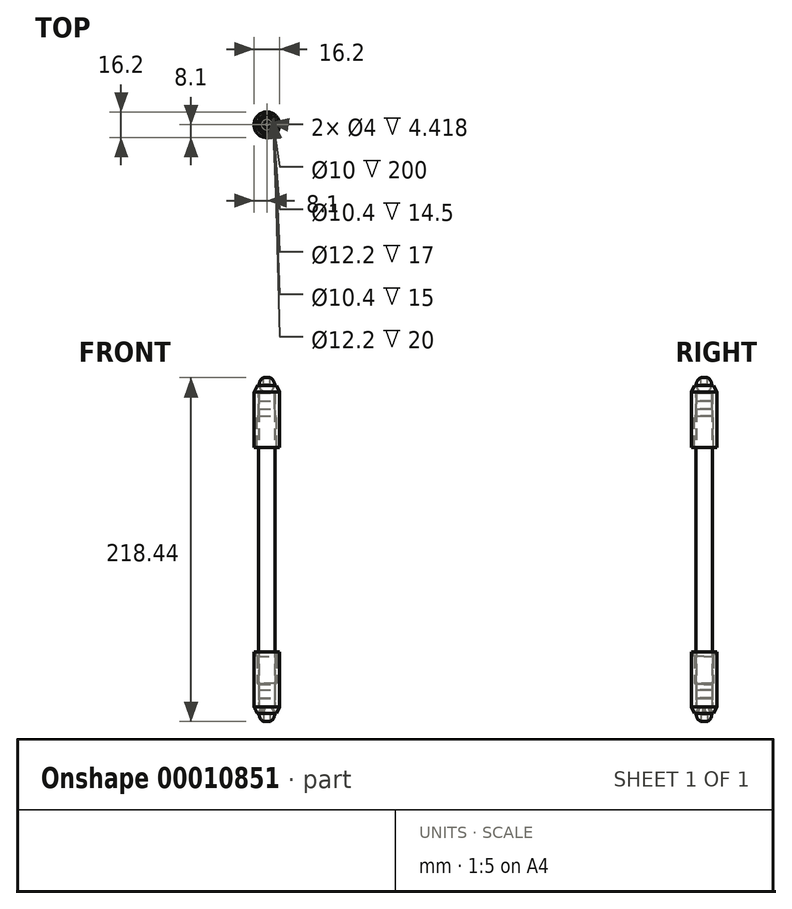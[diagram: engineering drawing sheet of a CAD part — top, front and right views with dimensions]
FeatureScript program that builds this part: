
annotation { "Feature Type Name" : "Feature", "Feature Type Description" : "" }
export const myFeature = defineFeature(function(context is Context, id is Id, definition is map)
    precondition{}
    {
        {
            var Q0;
            Q0=qCreatedBy(makeId("Front.planeOp"),FACE);
            var sketch = newSketch(context, id + "F0", { "sketchPlane" : qUnion([Q0])});
            skLineSegment(sketch, "E0", {"start": v(-5.03, 0.7) * mm, "end": v(-6.03, 0.7) * mm});
            skLineSegment(sketch, "E1", {"start": v(-8.1, 4.8) * mm, "end": v(-8.1, 39.8) * mm});
            skLineSegment(sketch, "E2", {"start": v(-8.1, 39.8) * mm, "end": v(-6.1, 39.8) * mm});
            skLineSegment(sketch, "E3", {"start": v(-6.1, 39.8) * mm, "end": v(-6.1, 19.8) * mm});
            skLineSegment(sketch, "E4", {"start": v(-6.1, 19.8) * mm, "end": v(-5.2, 19.8) * mm});
            skLineSegment(sketch, "E5", {"start": v(-5.2, 19.8) * mm, "end": v(-5.2, 4.8) * mm});
            skLineSegment(sketch, "E6", {"start": v(-5.2, 4.8) * mm, "end": v(-3.11, 4.8) * mm});
            skLineSegment(sketch, "E7", {"start": v(0, 5.2) * mm, "end": v(0, 4.8) * mm});
            skLineSegment(sketch, "E8", {"start": v(-6.03, 0.7) * mm, "end": v(-8.1, 4.8) * mm});
            skLineSegment(sketch, "E9", {"start": v(0, 0) * mm, "end": v(0, 32.36) * mm, "construction": true});
            skLineSegment(sketch, "E10", {"start": v(2.85, 3.2) * mm, "end": v(-9.79, 3.2) * mm, "construction": true});
            skCircle(sketch, "E11", {"center": v(0, 0) * mm, "radius": 4.85 * mm});
            skLineSegment(sketch, "E12", {"start": v(0, 4.8) * mm, "end": v(0, -4.85) * mm});
            skLineSegment(sketch, "E13", {"start": v(0, 15.55) * mm, "end": v(-5, 15.55) * mm});
            skLineSegment(sketch, "E14", {"start": v(-5, 15.55) * mm, "end": v(-5, 10.55) * mm});
            skLineSegment(sketch, "E15", {"start": v(-5, 10.55) * mm, "end": v(0, 10.55) * mm});
            skLineSegment(sketch, "E16", {"start": v(0, 10.55) * mm, "end": v(0, 15.55) * mm});
            skLineSegment(sketch, "E17", {"start": v(0, 5.3) * mm, "end": v(-5, 5.3) * mm});
            skLineSegment(sketch, "E18", {"start": v(-5, 5.3) * mm, "end": v(-5, 10.3) * mm});
            skLineSegment(sketch, "E19", {"start": v(-5, 10.3) * mm, "end": v(0, 10.3) * mm});
            skLineSegment(sketch, "E20", {"start": v(0, 10.3) * mm, "end": v(0, 5.3) * mm});
            skLineSegment(sketch, "E21", {"start": v(-4, 2.74) * mm, "end": v(4, 2.74) * mm, "construction": true});
            skLineSegment(sketch, "E22", {"start": v(0, 11.48) * mm, "end": v(-8.67, -7.13) * mm, "construction": true});
            skLineSegment(sketch, "E23", {"start": v(-5.03, 0.7) * mm, "end": v(-3.11, 4.8) * mm});
            skPoint(sketch, "E24", {"position": v(-4.4, 2.05) * mm});
            skSolve(sketch);
        }
        {
            var Q0;
            Q0=makeQuery(id+"F0.imprint","IMPRINT",FACE,{"disambiguationData":[TD([[makeQuery(id+"F0.imprint","IMPRINT",EDGE,{"derivedFrom":sQuery(id+"F0.wireOp",EDGE,"E13")}),1.0]])]});
            var Q1;
            Q1=makeQuery(id+"F0.imprint","IMPRINT",FACE,{"disambiguationData":[TD([[makeQuery(id+"F0.imprint","IMPRINT",EDGE,{"derivedFrom":sQuery(id+"F0.wireOp",EDGE,"E17")}),-1.0]])]});
            var Q2;
            {var subQ0=sQuery(id+"F0.wireOp",EDGE,"E12");Q2=makeQuery(id+"F0.imprint","IMPRINT",FACE,{"disambiguationData":[TD([[makeQuery(id+"F0.imprint","IMPRINT",EDGE,{"derivedFrom":subQ0}),-1.0]])]});}
            var Q3;
            {var subQ0=sQuery(id+"F0.wireOp",EDGE,"E0");Q3=makeQuery(id+"F0.imprint","IMPRINT",FACE,{"disambiguationData":[TD([[makeQuery(id+"F0.imprint","IMPRINT",EDGE,{"derivedFrom":subQ0}),-1.0]])]});}
            var Q4;
            Q4=sQuery(id+"F0.wireOp",EDGE,"E9");
            revolve(context, id + "F1", {"entities" : qUnion([Q0, Q1, Q2, Q3]), "axis" : qUnion([Q4]), "revolveType" : RevolveType.FULL});
        }
        {
            var Q0;
            Q0=makeQuery(id+"F1.opRevolve","SWEPT_FACE",FACE,{"disambiguationData":[OSD([sQuery(id+"F0.wireOp",EDGE,"E6")])]});
            var sketch = newSketch(context, id + "F2", { "sketchPlane" : qUnion([Q0])});
            skCircle(sketch, "E25", {"center": v(0, 0) * mm, "radius": 6 * mm});
            skCircle(sketch, "E26", {"center": v(0, 0) * mm, "radius": 5 * mm});
            skSolve(sketch);
        }
        {
            var Q0;
            Q0=makeQuery(id+"F2.imprint","IMPRINT",FACE,{"disambiguationData":[TD([[makeQuery(id+"F2.imprint","IMPRINT",EDGE,{"derivedFrom":sQuery(id+"F2.wireOp",EDGE,"E26")}),-1.0]])]});
            extrude(context, id + "F3", {"entities" : qUnion([Q0]), "depth" : 200 * mm});
        }
        {
            var Q0;
            Q0=makeQuery(id+"F3.opExtrude","CAP_FACE",FACE,{"disambiguationData":[OSD([sQuery(id+"F0.wireOp",EDGE,"E4"),sQuery(id+"F0.wireOp",EDGE,"E5"),sQuery(id+"F2.wireOp",EDGE,"E26")])],"isStart":false});
            cPlane(context, id + "F4", {"entities" : qUnion([Q0]), "cplaneType" : CPlaneType.OFFSET, "offset" : 100 * mm, "oppositeDirection" : true, "width" : 150 * mm, "height" : 150 * mm});
        }
        {
            var Q0;
            Q0=qCreatedBy(makeId("Top.planeOp"),FACE);
            cPlane(context, id + "F5", {"entities" : qUnion([Q0]), "cplaneType" : CPlaneType.OFFSET, "offset" : 5 * mm, "oppositeDirection" : true, "width" : 150 * mm, "height" : 150 * mm});
        }
        {
            var Q0;
            Q0=qCreatedBy(id+"F5.planeOp",FACE);
            var sketch = newSketch(context, id + "F6", { "sketchPlane" : qUnion([Q0])});
            skCircle(sketch, "E27", {"center": v(0, 0) * mm, "radius": 2 * mm});
            skSolve(sketch);
        }
        {
            var Q0;
            Q0=makeQuery(id+"F6.imprint","IMPRINT",FACE,{"disambiguationData":[TD([[makeQuery(id+"F6.imprint","IMPRINT",EDGE,{"derivedFrom":sQuery(id+"F6.wireOp",EDGE,"E27")}),1.0]])]});
            extrude(context, id + "F7", {"entities" : qUnion([Q0]), "operationType" : NewBodyOperationType.REMOVE, "depth" : 5 * mm});
        }
        {
            var Q0;
            Q0=makeQuery(id+"F1.opRevolve","SWEPT_BODY",BODY,{"disambiguationData":[OSD([sQuery(id+"F0.wireOp",EDGE,"E17"),sQuery(id+"F0.wireOp",EDGE,"E18"),sQuery(id+"F0.wireOp",EDGE,"E19"),sQuery(id+"F0.wireOp",EDGE,"E20")])]});
            var Q1;
            Q1=makeQuery(id+"F1.opRevolve","SWEPT_BODY",BODY,{"disambiguationData":[OSD([sQuery(id+"F0.wireOp",EDGE,"E13"),sQuery(id+"F0.wireOp",EDGE,"E14"),sQuery(id+"F0.wireOp",EDGE,"E15"),sQuery(id+"F0.wireOp",EDGE,"E16")])]});
            var Q2;
            Q2=makeQuery(id+"F1.opRevolve","SWEPT_BODY",BODY,{"disambiguationData":[OSD([sQuery(id+"F0.wireOp",EDGE,"E11"),sQuery(id+"F0.wireOp",EDGE,"E12")])]});
            var Q3;
            Q3=makeQuery(id+"F1.opRevolve","SWEPT_BODY",BODY,{"disambiguationData":[OSD([sQuery(id+"F0.wireOp",EDGE,"841e1b56-2235-48bc-aee3-342361c37d41"),sQuery(id+"F0.wireOp",EDGE,"E0"),sQuery(id+"F0.wireOp",EDGE,"E1"),sQuery(id+"F0.wireOp",EDGE,"E2"),sQuery(id+"F0.wireOp",EDGE,"E3"),sQuery(id+"F0.wireOp",EDGE,"E4"),sQuery(id+"F0.wireOp",EDGE,"E5"),sQuery(id+"F0.wireOp",EDGE,"E6"),sQuery(id+"F0.wireOp",EDGE,"E8"),sQuery(id+"F0.wireOp",EDGE,"4b548780-3497-4359-ae85-f4aefd225b06")])]});
            var Q4;
            Q4=qCreatedBy(id+"F4.planeOp",FACE);
            mirror(context, id + "F8", {"entities" : qUnion([Q0, Q1, Q2, Q3]), "mirrorPlane" : qUnion([Q4])});
        }
        {
            var Q0;
            Q0=makeQuery(id+"F1.opRevolve","SWEPT_EDGE",EDGE,{"disambiguationData":[OSD([sQuery(id+"F0.wireOp",EDGE,"E2"),sQuery(id+"F0.wireOp",EDGE,"E3")])]});
            var Q1;
            Q1=makeQuery(id+"F1.opRevolve","SWEPT_EDGE",EDGE,{"disambiguationData":[OSD([sQuery(id+"F0.wireOp",EDGE,"E2"),sQuery(id+"F0.wireOp",EDGE,"E3")])]});
            chamfer(context, id + "F9", {"entities" : qUnion([Q0, Q1]), "chamferType" : ChamferType.TWO_OFFSETS, "width1" : 1 * mm, "oppositeDirection" : false, "width2" : 3 * mm, "tangentPropagation" : true});
        }
        {
            var Q0;
            Q0=qCreatedBy(makeId("Front.planeOp"),FACE);
            var sketch = newSketch(context, id + "F10", { "sketchPlane" : qUnion([Q0])});
            skLineSegment(sketch, "E28", {"start": v(-5.5, 0.7) * mm, "end": v(-3.6, 4.8) * mm});
            skLineSegment(sketch, "E29", {"start": v(-5.5, 0.7) * mm, "end": v(-4.14, 0.7) * mm});
            skLineSegment(sketch, "E30", {"start": v(-4.14, 0.7) * mm, "end": v(-2.47, 4.8) * mm});
            skLineSegment(sketch, "E31", {"start": v(-2.47, 4.8) * mm, "end": v(-3.6, 4.8) * mm});
            skLineSegment(sketch, "E32", {"start": v(0, 0) * mm, "end": v(0, -5.1) * mm, "construction": true});
            skSolve(sketch);
        }
        {
            var Q0;
            Q0=makeQuery(id+"F10.imprint","IMPRINT",FACE,{"disambiguationData":[TD([[makeQuery(id+"F10.imprint","IMPRINT",EDGE,{"derivedFrom":sQuery(id+"F10.wireOp",EDGE,"E28")}),-1.0]])]});
            var Q1;
            Q1=sQuery(id+"F10.wireOp",EDGE,"E32");
            revolve(context, id + "F11", {"entities" : qUnion([Q0]), "axis" : qUnion([Q1]), "revolveType" : RevolveType.SYMMETRIC, "angle" : 108 * degree});
        }
        {
            var Q0;
            Q0=makeQuery(id+"F11.opRevolve","SWEPT_BODY",BODY,{"disambiguationData":[OSD([sQuery(id+"F10.wireOp",EDGE,"E28"),sQuery(id+"F10.wireOp",EDGE,"E29"),sQuery(id+"F10.wireOp",EDGE,"E30"),sQuery(id+"F10.wireOp",EDGE,"E31")])]});
            var Q1;
            Q1=sQuery(id+"F10.wireOp",EDGE,"E32");
            circularPattern(context, id + "F12", {"entities" : qUnion([Q0]), "axis" : qUnion([Q1]), "angle" : 120 * degree, "instanceCount" : 3, "computeTransformsWithoutBuiltin" : true});
        }
        {
            var Q0;
            Q0=makeQuery(id+"F11.opRevolve","SWEPT_BODY",BODY,{"disambiguationData":[OSD([sQuery(id+"F10.wireOp",EDGE,"E28"),sQuery(id+"F10.wireOp",EDGE,"E29"),sQuery(id+"F10.wireOp",EDGE,"E30"),sQuery(id+"F10.wireOp",EDGE,"E31")])]});
            var Q1;
            Q1=makeQuery(id+"F12.opPattern","COPY",BODY,{"derivedFrom":makeQuery(id+"F11.opRevolve","SWEPT_BODY",BODY,{"disambiguationData":[OSD([sQuery(id+"F10.wireOp",EDGE,"E28"),sQuery(id+"F10.wireOp",EDGE,"E29"),sQuery(id+"F10.wireOp",EDGE,"E30"),sQuery(id+"F10.wireOp",EDGE,"E31")])]}),"instanceName":"2"});
            var Q2;
            Q2=makeQuery(id+"F12.opPattern","COPY",BODY,{"derivedFrom":makeQuery(id+"F11.opRevolve","SWEPT_BODY",BODY,{"disambiguationData":[OSD([sQuery(id+"F10.wireOp",EDGE,"E28"),sQuery(id+"F10.wireOp",EDGE,"E29"),sQuery(id+"F10.wireOp",EDGE,"E30"),sQuery(id+"F10.wireOp",EDGE,"E31")])]}),"instanceName":"1"});
            var Q3;
            Q3=makeQuery(id+"F1.opRevolve","SWEPT_BODY",BODY,{"disambiguationData":[OSD([sQuery(id+"F0.wireOp",EDGE,"E0"),sQuery(id+"F0.wireOp",EDGE,"E1"),sQuery(id+"F0.wireOp",EDGE,"E2"),sQuery(id+"F0.wireOp",EDGE,"E3"),sQuery(id+"F0.wireOp",EDGE,"E5"),sQuery(id+"F0.wireOp",EDGE,"E6"),sQuery(id+"F0.wireOp",EDGE,"E8"),sQuery(id+"F0.wireOp",EDGE,"E23")])]});
            booleanBodies(context, id + "F13", {"operationType" : BooleanOperationType.SUBTRACTION, "tools" : qUnion([Q0, Q1, Q2]), "targets" : qUnion([Q3])});
        }
        {
            var Q0;
            Q0=makeQuery(id+"F13.opBoolean","COPY",EDGE,{"derivedFrom":makeQuery(id+"F11.opRevolve","CAP_EDGE",EDGE,{"disambiguationData":[OSD([sQuery(id+"F10.wireOp",EDGE,"E28")])],"isStart":true})});
            var Q1;
            Q1=makeQuery(id+"F13.opBoolean","COPY",EDGE,{"derivedFrom":makeQuery(id+"F12.opPattern","COPY",EDGE,{"derivedFrom":makeQuery(id+"F11.opRevolve","CAP_EDGE",EDGE,{"disambiguationData":[OSD([sQuery(id+"F10.wireOp",EDGE,"E28")])],"isStart":false}),"instanceName":"2"})});
            var Q2;
            Q2=makeQuery(id+"F13.opBoolean","COPY",EDGE,{"derivedFrom":makeQuery(id+"F12.opPattern","COPY",EDGE,{"derivedFrom":makeQuery(id+"F11.opRevolve","CAP_EDGE",EDGE,{"disambiguationData":[OSD([sQuery(id+"F10.wireOp",EDGE,"E28")])],"isStart":true}),"instanceName":"1"})});
            var Q3;
            Q3=makeQuery(id+"F13.opBoolean","COPY",EDGE,{"derivedFrom":makeQuery(id+"F11.opRevolve","CAP_EDGE",EDGE,{"disambiguationData":[OSD([sQuery(id+"F10.wireOp",EDGE,"E28")])],"isStart":false})});
            var Q4;
            Q4=makeQuery(id+"F13.opBoolean","COPY",EDGE,{"derivedFrom":makeQuery(id+"F12.opPattern","COPY",EDGE,{"derivedFrom":makeQuery(id+"F11.opRevolve","CAP_EDGE",EDGE,{"disambiguationData":[OSD([sQuery(id+"F10.wireOp",EDGE,"E28")])],"isStart":true}),"instanceName":"2"})});
            var Q5;
            Q5=makeQuery(id+"F13.opBoolean","COPY",EDGE,{"derivedFrom":makeQuery(id+"F12.opPattern","COPY",EDGE,{"derivedFrom":makeQuery(id+"F11.opRevolve","CAP_EDGE",EDGE,{"disambiguationData":[OSD([sQuery(id+"F10.wireOp",EDGE,"E28")])],"isStart":false}),"instanceName":"1"})});
            fillet(context, id + "F14", {"entities" : qUnion([Q0, Q1, Q2, Q3, Q4, Q5]), "radius" : 0.5 * mm, "tangentPropagation" : true, "allowEdgeOverflow" : false});
        }
        {
            var Q0;
            {var subQ0=sQuery(id+"F10.wireOp",EDGE,"E31");var subQ1=sQuery(id+"F10.wireOp",EDGE,"E30");var subQ2=sQuery(id+"F10.wireOp",EDGE,"E29");var subQ3=sQuery(id+"F10.wireOp",EDGE,"E28");Q0=makeQuery(id+"F14.opFillet","BLEND_EDGE",EDGE,{"blendedFrom":[makeQuery(id+"F13.opBoolean","COPY",EDGE,{"derivedFrom":makeQuery(id+"F11.opRevolve","CAP_EDGE",EDGE,{"disambiguationData":[OSD([subQ3])],"isStart":true})}),makeQuery(id+"F13.opBoolean","SPLIT",FACE,{"disambiguationData":[TD([makeQuery(id+"F11.opRevolve","CAP_FACE",FACE,{"disambiguationData":[OSD([subQ3,subQ2,subQ1,subQ0])],"isStart":true})])],"derivedFrom":makeQuery(id+"F1.opRevolve","SWEPT_FACE",FACE,{"disambiguationData":[OSD([sQuery(id+"F0.wireOp",EDGE,"E23")])]})})],"blendedInto":[makeQuery(id+"F13.opBoolean","SPLIT",FACE,{"disambiguationData":[TD([makeQuery(id+"F11.opRevolve","CAP_FACE",FACE,{"disambiguationData":[OSD([subQ3,subQ2,subQ1,subQ0])],"isStart":true})])],"derivedFrom":makeQuery(id+"F1.opRevolve","SWEPT_FACE",FACE,{"disambiguationData":[OSD([sQuery(id+"F0.wireOp",EDGE,"E23")])]})})]});}
            var Q1;
            {var subQ0=sQuery(id+"F10.wireOp",EDGE,"E31");var subQ1=sQuery(id+"F10.wireOp",EDGE,"E30");var subQ2=sQuery(id+"F10.wireOp",EDGE,"E29");var subQ3=sQuery(id+"F10.wireOp",EDGE,"E28");Q1=makeQuery(id+"F14.opFillet","BLEND_EDGE",EDGE,{"blendedFrom":[makeQuery(id+"F13.opBoolean","COPY",EDGE,{"derivedFrom":makeQuery(id+"F12.opPattern","COPY",EDGE,{"derivedFrom":makeQuery(id+"F11.opRevolve","CAP_EDGE",EDGE,{"disambiguationData":[OSD([subQ3])],"isStart":false}),"instanceName":"2"})}),makeQuery(id+"F13.opBoolean","SPLIT",FACE,{"disambiguationData":[TD([makeQuery(id+"F11.opRevolve","CAP_FACE",FACE,{"disambiguationData":[OSD([subQ3,subQ2,subQ1,subQ0])],"isStart":true})])],"derivedFrom":makeQuery(id+"F1.opRevolve","SWEPT_FACE",FACE,{"disambiguationData":[OSD([sQuery(id+"F0.wireOp",EDGE,"E23")])]})})],"blendedInto":[makeQuery(id+"F13.opBoolean","SPLIT",FACE,{"disambiguationData":[TD([makeQuery(id+"F11.opRevolve","CAP_FACE",FACE,{"disambiguationData":[OSD([subQ3,subQ2,subQ1,subQ0])],"isStart":true})])],"derivedFrom":makeQuery(id+"F1.opRevolve","SWEPT_FACE",FACE,{"disambiguationData":[OSD([sQuery(id+"F0.wireOp",EDGE,"E23")])]})})]});}
            var Q2;
            {var subQ0=sQuery(id+"F10.wireOp",EDGE,"E31");var subQ1=sQuery(id+"F10.wireOp",EDGE,"E30");var subQ2=sQuery(id+"F10.wireOp",EDGE,"E29");var subQ3=sQuery(id+"F10.wireOp",EDGE,"E28");Q2=makeQuery(id+"F14.opFillet","BLEND_EDGE",EDGE,{"blendedFrom":[makeQuery(id+"F13.opBoolean","COPY",EDGE,{"derivedFrom":makeQuery(id+"F12.opPattern","COPY",EDGE,{"derivedFrom":makeQuery(id+"F11.opRevolve","CAP_EDGE",EDGE,{"disambiguationData":[OSD([subQ3])],"isStart":true}),"instanceName":"1"})}),makeQuery(id+"F13.opBoolean","SPLIT",FACE,{"disambiguationData":[TD([makeQuery(id+"F11.opRevolve","CAP_FACE",FACE,{"disambiguationData":[OSD([subQ3,subQ2,subQ1,subQ0])],"isStart":false})])],"derivedFrom":makeQuery(id+"F1.opRevolve","SWEPT_FACE",FACE,{"disambiguationData":[OSD([sQuery(id+"F0.wireOp",EDGE,"E23")])]})})],"blendedInto":[makeQuery(id+"F13.opBoolean","SPLIT",FACE,{"disambiguationData":[TD([makeQuery(id+"F11.opRevolve","CAP_FACE",FACE,{"disambiguationData":[OSD([subQ3,subQ2,subQ1,subQ0])],"isStart":false})])],"derivedFrom":makeQuery(id+"F1.opRevolve","SWEPT_FACE",FACE,{"disambiguationData":[OSD([sQuery(id+"F0.wireOp",EDGE,"E23")])]})})]});}
            var Q3;
            {var subQ0=sQuery(id+"F10.wireOp",EDGE,"E31");var subQ1=sQuery(id+"F10.wireOp",EDGE,"E30");var subQ2=sQuery(id+"F10.wireOp",EDGE,"E29");var subQ3=sQuery(id+"F10.wireOp",EDGE,"E28");Q3=makeQuery(id+"F14.opFillet","BLEND_EDGE",EDGE,{"blendedFrom":[makeQuery(id+"F13.opBoolean","COPY",EDGE,{"derivedFrom":makeQuery(id+"F11.opRevolve","CAP_EDGE",EDGE,{"disambiguationData":[OSD([subQ3])],"isStart":false})}),makeQuery(id+"F13.opBoolean","SPLIT",FACE,{"disambiguationData":[TD([makeQuery(id+"F11.opRevolve","CAP_FACE",FACE,{"disambiguationData":[OSD([subQ3,subQ2,subQ1,subQ0])],"isStart":false})])],"derivedFrom":makeQuery(id+"F1.opRevolve","SWEPT_FACE",FACE,{"disambiguationData":[OSD([sQuery(id+"F0.wireOp",EDGE,"E23")])]})})],"blendedInto":[makeQuery(id+"F13.opBoolean","SPLIT",FACE,{"disambiguationData":[TD([makeQuery(id+"F11.opRevolve","CAP_FACE",FACE,{"disambiguationData":[OSD([subQ3,subQ2,subQ1,subQ0])],"isStart":false})])],"derivedFrom":makeQuery(id+"F1.opRevolve","SWEPT_FACE",FACE,{"disambiguationData":[OSD([sQuery(id+"F0.wireOp",EDGE,"E23")])]})})]});}
            var Q4;
            {var subQ0=sQuery(id+"F10.wireOp",EDGE,"E31");var subQ1=sQuery(id+"F10.wireOp",EDGE,"E30");var subQ2=sQuery(id+"F10.wireOp",EDGE,"E29");var subQ3=sQuery(id+"F10.wireOp",EDGE,"E28");Q4=makeQuery(id+"F14.opFillet","BLEND_EDGE",EDGE,{"blendedFrom":[makeQuery(id+"F13.opBoolean","COPY",EDGE,{"derivedFrom":makeQuery(id+"F12.opPattern","COPY",EDGE,{"derivedFrom":makeQuery(id+"F11.opRevolve","CAP_EDGE",EDGE,{"disambiguationData":[OSD([subQ3])],"isStart":false}),"instanceName":"1"})}),makeQuery(id+"F13.opBoolean","SPLIT",FACE,{"disambiguationData":[TD([makeQuery(id+"F12.opPattern","COPY",FACE,{"derivedFrom":makeQuery(id+"F11.opRevolve","CAP_FACE",FACE,{"disambiguationData":[OSD([subQ3,subQ2,subQ1,subQ0])],"isStart":false}),"instanceName":"1"})])],"derivedFrom":makeQuery(id+"F1.opRevolve","SWEPT_FACE",FACE,{"disambiguationData":[OSD([sQuery(id+"F0.wireOp",EDGE,"E23")])]})})],"blendedInto":[makeQuery(id+"F13.opBoolean","SPLIT",FACE,{"disambiguationData":[TD([makeQuery(id+"F12.opPattern","COPY",FACE,{"derivedFrom":makeQuery(id+"F11.opRevolve","CAP_FACE",FACE,{"disambiguationData":[OSD([subQ3,subQ2,subQ1,subQ0])],"isStart":false}),"instanceName":"1"})])],"derivedFrom":makeQuery(id+"F1.opRevolve","SWEPT_FACE",FACE,{"disambiguationData":[OSD([sQuery(id+"F0.wireOp",EDGE,"E23")])]})})]});}
            var Q5;
            {var subQ0=sQuery(id+"F10.wireOp",EDGE,"E31");var subQ1=sQuery(id+"F10.wireOp",EDGE,"E30");var subQ2=sQuery(id+"F10.wireOp",EDGE,"E29");var subQ3=sQuery(id+"F10.wireOp",EDGE,"E28");Q5=makeQuery(id+"F14.opFillet","BLEND_EDGE",EDGE,{"blendedFrom":[makeQuery(id+"F13.opBoolean","COPY",EDGE,{"derivedFrom":makeQuery(id+"F12.opPattern","COPY",EDGE,{"derivedFrom":makeQuery(id+"F11.opRevolve","CAP_EDGE",EDGE,{"disambiguationData":[OSD([subQ3])],"isStart":true}),"instanceName":"2"})}),makeQuery(id+"F13.opBoolean","SPLIT",FACE,{"disambiguationData":[TD([makeQuery(id+"F12.opPattern","COPY",FACE,{"derivedFrom":makeQuery(id+"F11.opRevolve","CAP_FACE",FACE,{"disambiguationData":[OSD([subQ3,subQ2,subQ1,subQ0])],"isStart":false}),"instanceName":"1"})])],"derivedFrom":makeQuery(id+"F1.opRevolve","SWEPT_FACE",FACE,{"disambiguationData":[OSD([sQuery(id+"F0.wireOp",EDGE,"E23")])]})})],"blendedInto":[makeQuery(id+"F13.opBoolean","SPLIT",FACE,{"disambiguationData":[TD([makeQuery(id+"F12.opPattern","COPY",FACE,{"derivedFrom":makeQuery(id+"F11.opRevolve","CAP_FACE",FACE,{"disambiguationData":[OSD([subQ3,subQ2,subQ1,subQ0])],"isStart":false}),"instanceName":"1"})])],"derivedFrom":makeQuery(id+"F1.opRevolve","SWEPT_FACE",FACE,{"disambiguationData":[OSD([sQuery(id+"F0.wireOp",EDGE,"E23")])]})})]});}
            fillet(context, id + "F15", {"entities" : qUnion([Q0, Q1, Q2, Q3, Q4, Q5]), "radius" : 0.5 * mm, "tangentPropagation" : true, "allowEdgeOverflow" : false});
        }
        {
            var Q0;
            Q0=makeQuery(id+"F1.opRevolve","SWEPT_EDGE",EDGE,{"disambiguationData":[OSD([sQuery(id+"F0.wireOp",EDGE,"E4"),sQuery(id+"F0.wireOp",EDGE,"E5")])]});
            chamfer(context, id + "F16", {"entities" : qUnion([Q0]), "width" : 0.5 * mm, "tangentPropagation" : true});
        }
    });
